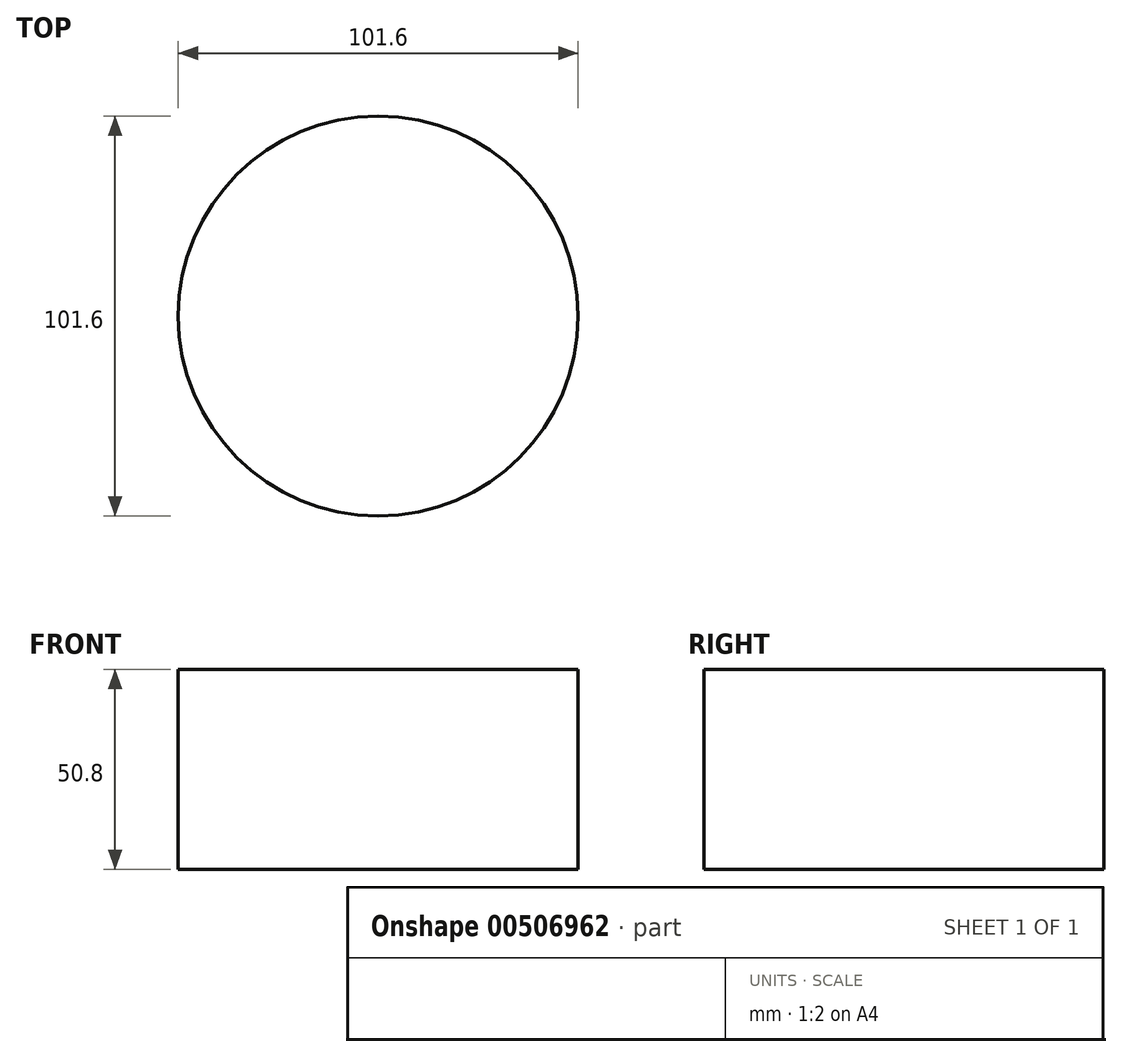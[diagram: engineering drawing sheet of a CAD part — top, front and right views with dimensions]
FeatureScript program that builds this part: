
annotation { "Feature Type Name" : "Feature", "Feature Type Description" : "" }
export const myFeature = defineFeature(function(context is Context, id is Id, definition is map)
    precondition{}
    {
        {
            var Q0;
            Q0=qCreatedBy(makeId("Front.planeOp"),FACE);
            var sketch = newSketch(context, id + "F0", { "sketchPlane" : qUnion([Q0])});
            skLineSegment(sketch, "E0", {"start": v(0, 0) * mm, "end": v(50.8, 0) * mm});
            skLineSegment(sketch, "E1", {"start": v(50.8, 0) * mm, "end": v(50.8, 50.8) * mm});
            skLineSegment(sketch, "E2", {"start": v(50.8, 50.8) * mm, "end": v(0, 50.8) * mm});
            skLineSegment(sketch, "E3", {"start": v(0, 50.8) * mm, "end": v(0, 0) * mm});
            skSolve(sketch);
        }
        {
            var Q0;
            Q0=makeQuery(id+"F0.imprint","IMPRINT",FACE,{"disambiguationData":[TD([[makeQuery(id+"F0.imprint","IMPRINT",EDGE,{"derivedFrom":sQuery(id+"F0.wireOp",EDGE,"E0")}),1.0]])]});
            var Q1;
            Q1=sQuery(id+"F0.wireOp",EDGE,"E3");
            revolve(context, id + "F1", {"entities" : qUnion([Q0]), "axis" : qUnion([Q1]), "revolveType" : RevolveType.SYMMETRIC, "angle" : 360 * degree});
        }
    });
